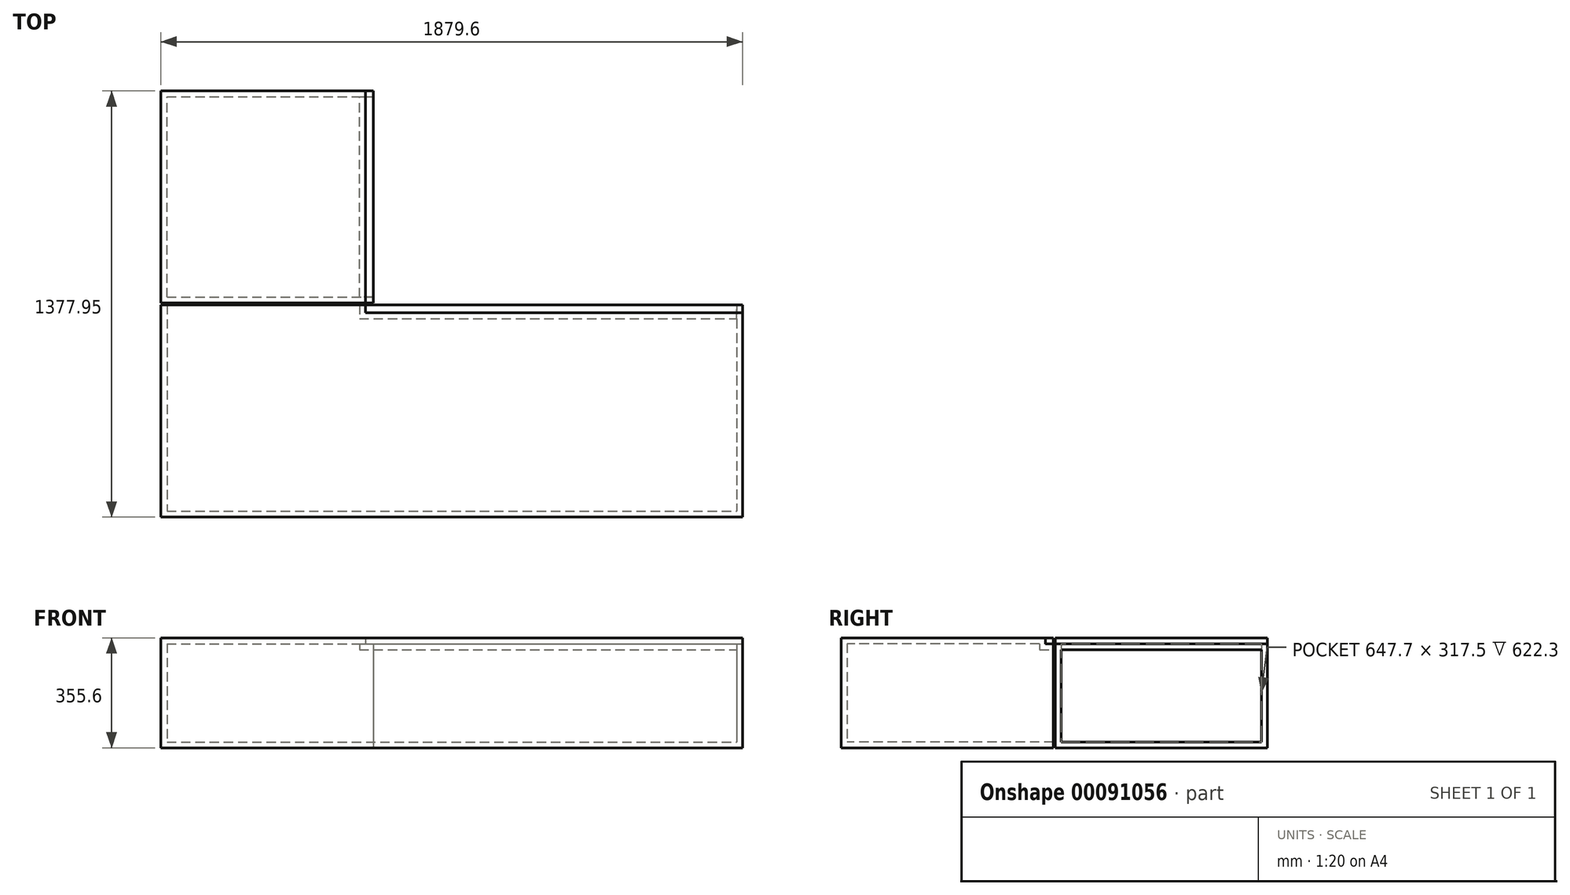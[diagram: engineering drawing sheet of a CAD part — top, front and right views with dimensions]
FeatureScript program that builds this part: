
annotation { "Feature Type Name" : "Feature", "Feature Type Description" : "" }
export const myFeature = defineFeature(function(context is Context, id is Id, definition is map)
    precondition{}
    {
        {
            var Q0;
            Q0=qCreatedBy(makeId("Top.planeOp"),FACE);
            var sketch = newSketch(context, id + "F0", { "sketchPlane" : qUnion([Q0])});
            skLineSegment(sketch, "E0.bottom", {"start": v(-731.3, 337.53) * mm, "end": v(1148.3, 337.53) * mm});
            skLineSegment(sketch, "E0.top", {"start": v(-731.3, -348.27) * mm, "end": v(1148.3, -348.27) * mm});
            skLineSegment(sketch, "E0.left", {"start": v(-731.3, 337.53) * mm, "end": v(-731.3, -348.27) * mm});
            skLineSegment(sketch, "E0.right", {"start": v(1148.3, 337.53) * mm, "end": v(1148.3, -348.27) * mm});
            skSolve(sketch);
        }
        {
            var Q0;
            Q0 = qSketchRegion(id + "F0", true);
            extrude(context, id + "F1", {"entities" : qUnion([Q0]), "depth" : 355.6 * mm});
        }
        {
            var Q0;
            Q0=makeQuery(id+"F1.opExtrude","SWEPT_FACE",FACE,{"disambiguationData":[OSD([sQuery(id+"F0.wireOp",EDGE,"E0.right")])]});
            var sketch = newSketch(context, id + "F2", { "sketchPlane" : qUnion([Q0])});
            skLineSegment(sketch, "E1", {"start": v(337.53, 355.6) * mm, "end": v(312.13, 355.6) * mm});
            skLineSegment(sketch, "E2", {"start": v(312.13, 355.6) * mm, "end": v(312.13, 336.55) * mm});
            skLineSegment(sketch, "E3", {"start": v(312.13, 336.55) * mm, "end": v(337.53, 336.55) * mm});
            skLineSegment(sketch, "E4", {"start": v(337.53, 336.55) * mm, "end": v(337.53, 355.6) * mm});
            skSolve(sketch);
        }
        {
            var Q0;
            Q0 = qSketchRegion(id + "F2", true);
            var Q1;
            Q1=makeQuery(id+"F1.opExtrude","SWEPT_FACE",FACE,{"disambiguationData":[OSD([sQuery(id+"F0.wireOp",EDGE,"E0.left")])]});
            extrude(context, id + "F3", {"entities" : qUnion([Q0]), "operationType" : NewBodyOperationType.REMOVE, "oppositeDirection" : true, "endBoundEntityFace" : qUnion([Q1]), "depth" : 1219.2 * mm});
        }
        {
            var Q0;
            Q0=makeQuery(id+"F1.opExtrude","SWEPT_FACE",FACE,{"disambiguationData":[OSD([sQuery(id+"F0.wireOp",EDGE,"E0.bottom")])]});
            shell(context, id + "F4", {"entities" : qUnion([Q0]), "thickness" : 19.05 * mm});
        }
        {
            var Q0;
            Q0=makeQuery(id+"F1.opExtrude","CAP_FACE",FACE,{"disambiguationData":[OSD([sQuery(id+"F0.wireOp",EDGE,"E0.bottom"),sQuery(id+"F0.wireOp",EDGE,"E0.top"),sQuery(id+"F0.wireOp",EDGE,"E0.left"),sQuery(id+"F0.wireOp",EDGE,"E0.right")])],"isStart":true});
            var sketch = newSketch(context, id + "F5", { "sketchPlane" : qUnion([Q0])});
            skLineSegment(sketch, "E5.bottom", {"start": v(-731.3, -343.88) * mm, "end": v(-45.5, -343.88) * mm});
            skLineSegment(sketch, "E5.left", {"start": v(-731.3, -343.88) * mm, "end": v(-731.3, -1029.68) * mm});
            skLineSegment(sketch, "E5.right", {"start": v(-45.5, -343.88) * mm, "end": v(-45.5, -1029.68) * mm});
            skLineSegment(sketch, "E6", {"start": v(-731.3, -1029.68) * mm, "end": v(-45.5, -1029.68) * mm});
            skPoint(sketch, "E5.top.end.orphan", {"position": v(-45.5, -1715.48) * mm});
            skPoint(sketch, "E5.top.start.orphan", {"position": v(-731.3, -1715.48) * mm});
            skSolve(sketch);
        }
        {
            var Q0;
            {var subQ0=sQuery(id+"F5.wireOp",EDGE,"E5.bottom");Q0=makeQuery(id+"F5.imprint","IMPRINT",FACE,{"disambiguationData":[TD([[makeQuery(id+"F5.imprint","IMPRINT",EDGE,{"derivedFrom":subQ0}),-1.0]])]});}
            extrude(context, id + "F6", {"entities" : qUnion([Q0]), "oppositeDirection" : true, "depth" : 355.6 * mm});
        }
        {
            var Q0;
            Q0=makeQuery(id+"F6.opExtrude","SWEPT_FACE",FACE,{"disambiguationData":[OSD([sQuery(id+"F5.wireOp",EDGE,"E6")])]});
            var sketch = newSketch(context, id + "F7", { "sketchPlane" : qUnion([Q0])});
            skLineSegment(sketch, "E7", {"start": v(45.5, 355.6) * mm, "end": v(70.9, 355.6) * mm});
            skLineSegment(sketch, "E8", {"start": v(70.9, 355.6) * mm, "end": v(70.9, 336.55) * mm});
            skLineSegment(sketch, "E9", {"start": v(70.9, 336.55) * mm, "end": v(45.5, 336.55) * mm});
            skLineSegment(sketch, "E10", {"start": v(45.5, 336.55) * mm, "end": v(45.5, 355.6) * mm});
            skSolve(sketch);
        }
        {
            var Q0;
            Q0 = qSketchRegion(id + "F7", true);
            extrude(context, id + "F8", {"entities" : qUnion([Q0]), "operationType" : NewBodyOperationType.REMOVE, "endBound" : BoundingType.UP_TO_NEXT, "oppositeDirection" : true, "depth" : 25.4 * mm});
        }
        {
            var Q0;
            Q0=makeQuery(id+"F6.opExtrude","SWEPT_FACE",FACE,{"disambiguationData":[OSD([sQuery(id+"F5.wireOp",EDGE,"E5.right")])]});
            shell(context, id + "F9", {"entities" : qUnion([Q0]), "thickness" : 19.05 * mm});
        }
    });
